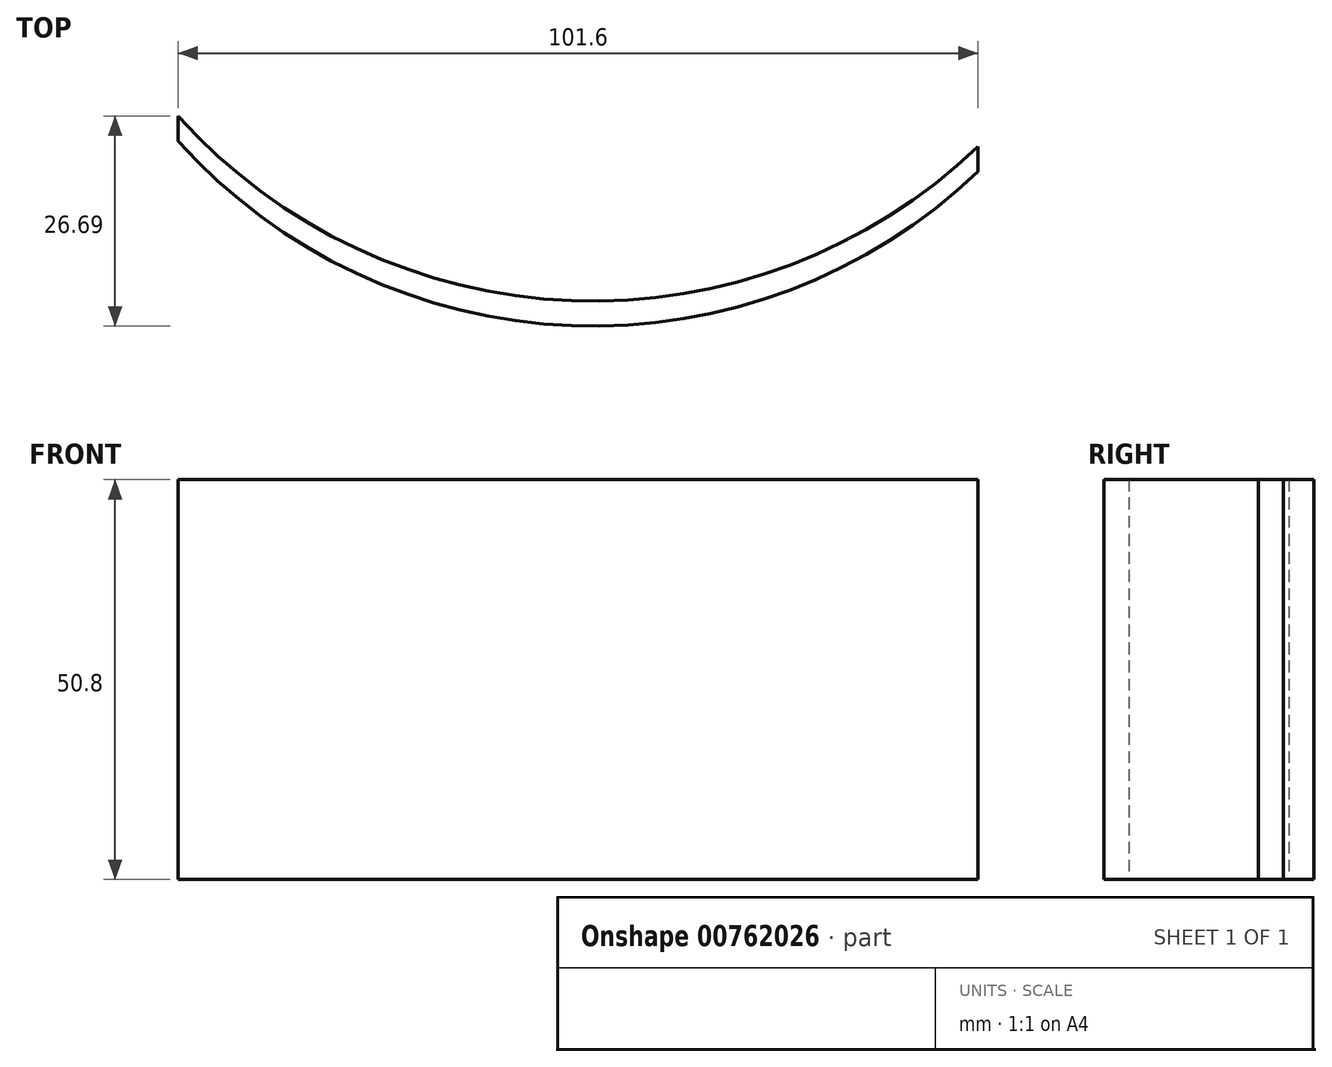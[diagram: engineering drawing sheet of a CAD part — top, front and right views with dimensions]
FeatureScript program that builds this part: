
annotation { "Feature Type Name" : "Feature", "Feature Type Description" : "" }
export const myFeature = defineFeature(function(context is Context, id is Id, definition is map)
    precondition{}
    {
        {
            var Q0;
            Q0=qCreatedBy(makeId("Top.planeOp"),FACE);
            var sketch = newSketch(context, id + "F0", { "sketchPlane" : qUnion([Q0])});
            skArc(sketch, "E0", {"start": v(-69.54, 39.9) * mm, "mid": v(-19.57, 16.45) * mm, "end": v(32.06, 36) * mm});
            skArc(sketch, "E1", {"start": v(-69.54, 36.73) * mm, "mid": v(-19.57, 13.28) * mm, "end": v(32.06, 32.82) * mm});
            skLineSegment(sketch, "E2", {"start": v(32.06, 32.82) * mm, "end": v(32.06, 36) * mm});
            skLineSegment(sketch, "E3", {"start": v(-69.54, 36.73) * mm, "end": v(-69.54, 39.9) * mm});
            skSolve(sketch);
        }
        {
            var Q0;
            Q0=makeQuery(id+"F0.imprint","IMPRINT",FACE,{"disambiguationData":[TD([[makeQuery(id+"F0.imprint","IMPRINT",EDGE,{"derivedFrom":sQuery(id+"F0.wireOp",EDGE,"E0")}),-1.0]])]});
            extrude(context, id + "F1", {"entities" : qUnion([Q0]), "depth" : 50.8 * mm, "offsetDistance" : 25.4 * mm});
        }
    });
